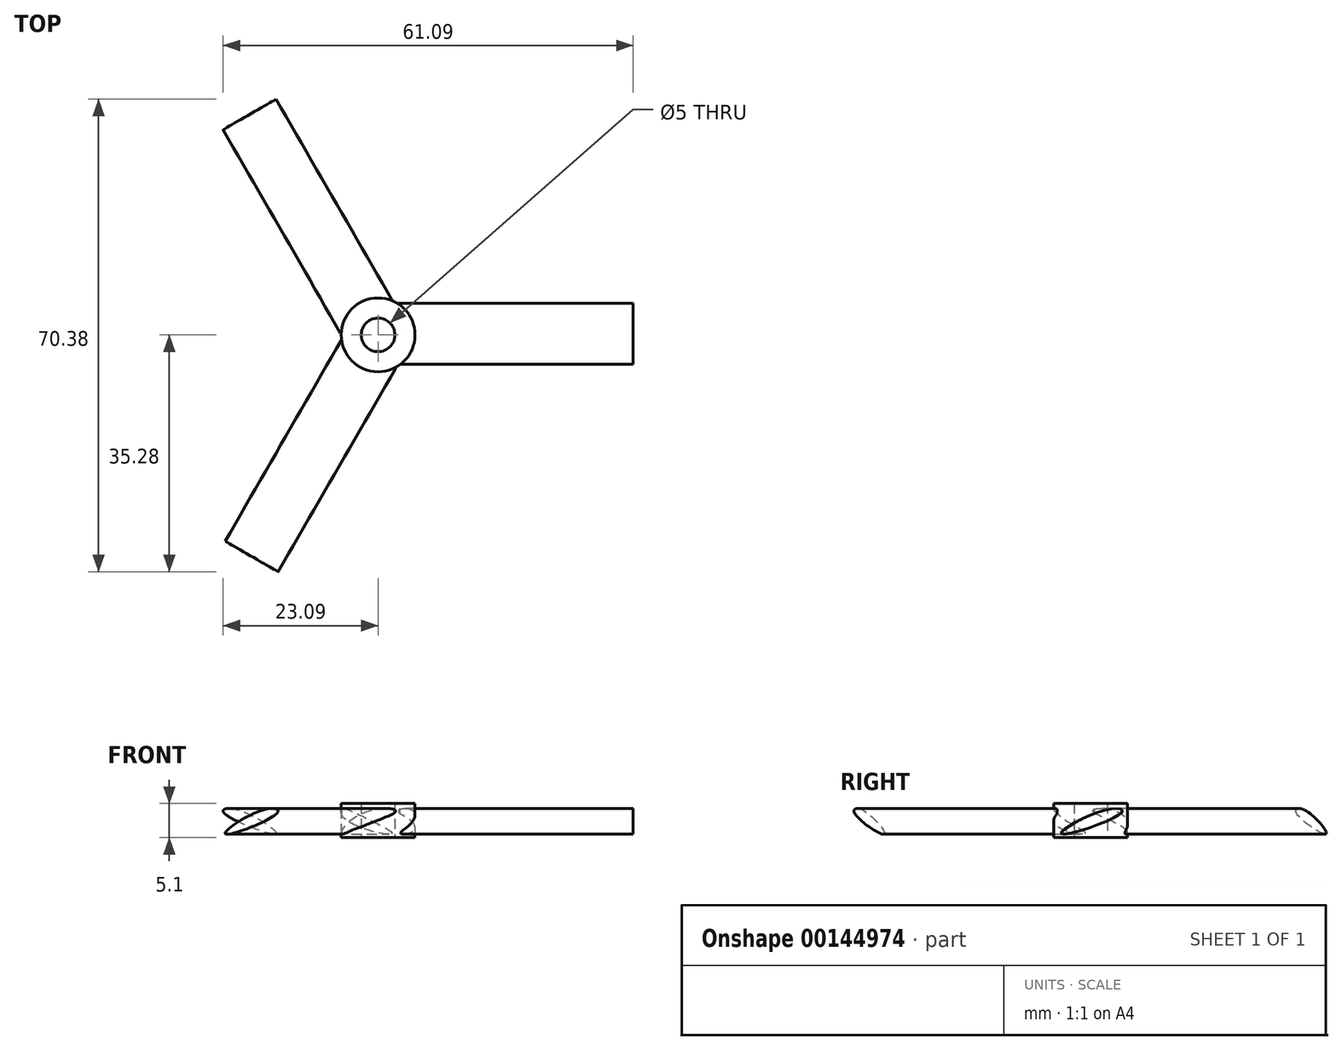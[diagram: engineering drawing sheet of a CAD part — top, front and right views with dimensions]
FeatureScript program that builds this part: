
annotation { "Feature Type Name" : "Feature", "Feature Type Description" : "" }
export const myFeature = defineFeature(function(context is Context, id is Id, definition is map)
    precondition{}
    {
        {
            var Q0;
            Q0=qCreatedBy(makeId("Top.planeOp"),FACE);
            var sketch = newSketch(context, id + "F0", { "sketchPlane" : qUnion([Q0])});
            skCircle(sketch, "E0", {"center": v(0, 0) * mm, "radius": 5.5 * mm, "construction": true});
            skCircle(sketch, "E1", {"center": v(0, 0) * mm, "radius": 2.5 * mm});
            skLineSegment(sketch, "E2.bottom", {"start": v(2.3, 5) * mm, "end": v(38, 5) * mm});
            skLineSegment(sketch, "E2.top", {"start": v(2.3, -5) * mm, "end": v(38, -5) * mm});
            skLineSegment(sketch, "E2.right", {"start": v(38, 5) * mm, "end": v(38, -5) * mm});
            skLineSegment(sketch, "E3.1.0", {"start": v(-5.48, 0.52) * mm, "end": v(-23.33, -30.4) * mm});
            skLineSegment(sketch, "E3.1.1", {"start": v(-14.67, -35.4) * mm, "end": v(-23.33, -30.4) * mm});
            skLineSegment(sketch, "E3.1.2", {"start": v(3.18, -4.48) * mm, "end": v(-14.67, -35.4) * mm});
            skLineSegment(sketch, "E3.2.0", {"start": v(3.18, 4.48) * mm, "end": v(-14.67, 35.4) * mm});
            skLineSegment(sketch, "E3.2.1", {"start": v(-23.33, 30.4) * mm, "end": v(-14.67, 35.4) * mm});
            skLineSegment(sketch, "E3.2.2", {"start": v(-5.48, -0.52) * mm, "end": v(-23.33, 30.4) * mm});
            skLineSegment(sketch, "E3.anchor1", {"start": v(0, 0) * mm, "end": v(2.3, -5) * mm, "construction": true});
            skLineSegment(sketch, "E3.anchor2", {"start": v(0, 0) * mm, "end": v(3.18, 4.48) * mm, "construction": true});
            skLineSegment(sketch, "E4", {"start": v(2.3, -5) * mm, "end": v(3.18, 4.48) * mm});
            skSolve(sketch);
        }
        {
            var Q0;
            Q0 = qSketchRegion(id + "F0", true);
            extrude(context, id + "F1", {"entities" : qUnion([Q0]), "depth" : 5 * mm});
        }
        {
            var Q0;
            Q0=makeQuery(id+"F1.opExtrude","SWEPT_FACE",FACE,{"disambiguationData":[OSD([sQuery(id+"F0.wireOp",EDGE,"E2.right")])]});
            var sketch = newSketch(context, id + "F2", { "sketchPlane" : qUnion([Q0])});
            skFitSpline(sketch, "E5", {"points": [v(4.63, 3.75) * mm, v(2.35, 4.17) * mm, v(-4.32, 0.56) * mm, v(4.63, 3.75) * mm]});
            skLineSegment(sketch, "E6.bottom", {"start": v(-5, 5) * mm, "end": v(5, 5) * mm});
            skLineSegment(sketch, "E6.top", {"start": v(-5, 0) * mm, "end": v(5, 0) * mm});
            skLineSegment(sketch, "E6.left", {"start": v(-5, 5) * mm, "end": v(-5, 0) * mm});
            skLineSegment(sketch, "E6.right", {"start": v(5, 5) * mm, "end": v(5, 0) * mm});
            skSolve(sketch);
        }
        {
            var Q0;
            Q0 = qSketchRegion(id + "F2", true);
            extrude(context, id + "F3", {"entities" : qUnion([Q0]), "operationType" : NewBodyOperationType.REMOVE, "oppositeDirection" : true, "depth" : 36 * mm});
        }
        {
            var Q0;
            Q0=makeQuery(id+"F1.opExtrude","SWEPT_FACE",FACE,{"disambiguationData":[OSD([sQuery(id+"F0.wireOp",EDGE,"E3.2.1")])]});
            var sketch = newSketch(context, id + "F4", { "sketchPlane" : qUnion([Q0])});
            skFitSpline(sketch, "E7", {"points": [v(4.62, 3.75) * mm, v(2.34, 4.17) * mm, v(-4.32, 0.57) * mm, v(4.62, 3.75) * mm]});
            skLineSegment(sketch, "E8.bottom", {"start": v(-5, 5) * mm, "end": v(5, 5) * mm});
            skLineSegment(sketch, "E8.top", {"start": v(-5, 0) * mm, "end": v(5, 0) * mm});
            skLineSegment(sketch, "E8.left", {"start": v(-5, 5) * mm, "end": v(-5, 0) * mm});
            skLineSegment(sketch, "E8.right", {"start": v(5, 5) * mm, "end": v(5, 0) * mm});
            skSolve(sketch);
        }
        {
            var Q0;
            Q0=makeQuery(id+"F4.imprint","IMPRINT",FACE,{"disambiguationData":[TD([[makeQuery(id+"F4.imprint","IMPRINT",EDGE,{"derivedFrom":sQuery(id+"F4.wireOp",EDGE,"E7")}),-1.0]])]});
            var Q1;
            Q1=sQuery(id+"F4.wireOp",EDGE,"E7");
            var Q2;
            Q2=sQuery(id+"F4.wireOp",EDGE,"E8.bottom");
            var Q3;
            Q3=sQuery(id+"F4.wireOp",EDGE,"E8.top");
            var Q4;
            Q4=sQuery(id+"F4.wireOp",EDGE,"E8.left");
            var Q5;
            Q5=sQuery(id+"F4.wireOp",EDGE,"E8.right");
            extrude(context, id + "F5", {"entities" : qUnion([Q0]), "operationType" : NewBodyOperationType.REMOVE, "surfaceEntities" : qUnion([Q1, Q2, Q3, Q4, Q5]), "oppositeDirection" : true, "depth" : 36 * mm});
        }
        {
            var Q0;
            Q0=makeQuery(id+"F1.opExtrude","SWEPT_FACE",FACE,{"disambiguationData":[OSD([sQuery(id+"F0.wireOp",EDGE,"E3.1.1")])]});
            var sketch = newSketch(context, id + "F6", { "sketchPlane" : qUnion([Q0])});
            skFitSpline(sketch, "E9", {"points": [v(4.65, 3.74) * mm, v(2.37, 4.16) * mm, v(-4.3, 0.55) * mm, v(4.65, 3.74) * mm]});
            skLineSegment(sketch, "E10.bottom", {"start": v(-5, 5) * mm, "end": v(5.03, 5) * mm});
            skLineSegment(sketch, "E10.top", {"start": v(-5, -0.01) * mm, "end": v(5.03, -0.01) * mm});
            skLineSegment(sketch, "E10.left", {"start": v(-5, 5) * mm, "end": v(-5, -0.01) * mm});
            skLineSegment(sketch, "E10.right", {"start": v(5.03, 5) * mm, "end": v(5.03, -0.01) * mm});
            skSolve(sketch);
        }
        {
            var Q0;
            Q0=makeQuery(id+"F6.imprint","IMPRINT",FACE,{"disambiguationData":[TD([[makeQuery(id+"F6.imprint","IMPRINT",EDGE,{"derivedFrom":sQuery(id+"F6.wireOp",EDGE,"E9")}),-1.0]])]});
            var Q1;
            Q1=sQuery(id+"F6.wireOp",EDGE,"E9");
            var Q2;
            Q2=sQuery(id+"F6.wireOp",EDGE,"E10.bottom");
            var Q3;
            Q3=sQuery(id+"F6.wireOp",EDGE,"E10.top");
            var Q4;
            Q4=sQuery(id+"F6.wireOp",EDGE,"E10.left");
            var Q5;
            Q5=sQuery(id+"F6.wireOp",EDGE,"E10.right");
            extrude(context, id + "F7", {"entities" : qUnion([Q0]), "operationType" : NewBodyOperationType.REMOVE, "surfaceEntities" : qUnion([Q1, Q2, Q3, Q4, Q5]), "oppositeDirection" : true, "depth" : 37 * mm});
        }
        {
            var Q0;
            Q0=qCreatedBy(makeId("Top.planeOp"),FACE);
            var sketch = newSketch(context, id + "F8", { "sketchPlane" : qUnion([Q0])});
            skCircle(sketch, "E11", {"center": v(0, 0) * mm, "radius": 5.5 * mm});
            skCircle(sketch, "E12", {"center": v(0, 0) * mm, "radius": 2.5 * mm});
            skSolve(sketch);
        }
        {
            var Q0;
            Q0 = qSketchRegion(id + "F8", true);
            extrude(context, id + "F9", {"entities" : qUnion([Q0]), "operationType" : NewBodyOperationType.ADD, "depth" : 5.1 * mm});
        }
    });
